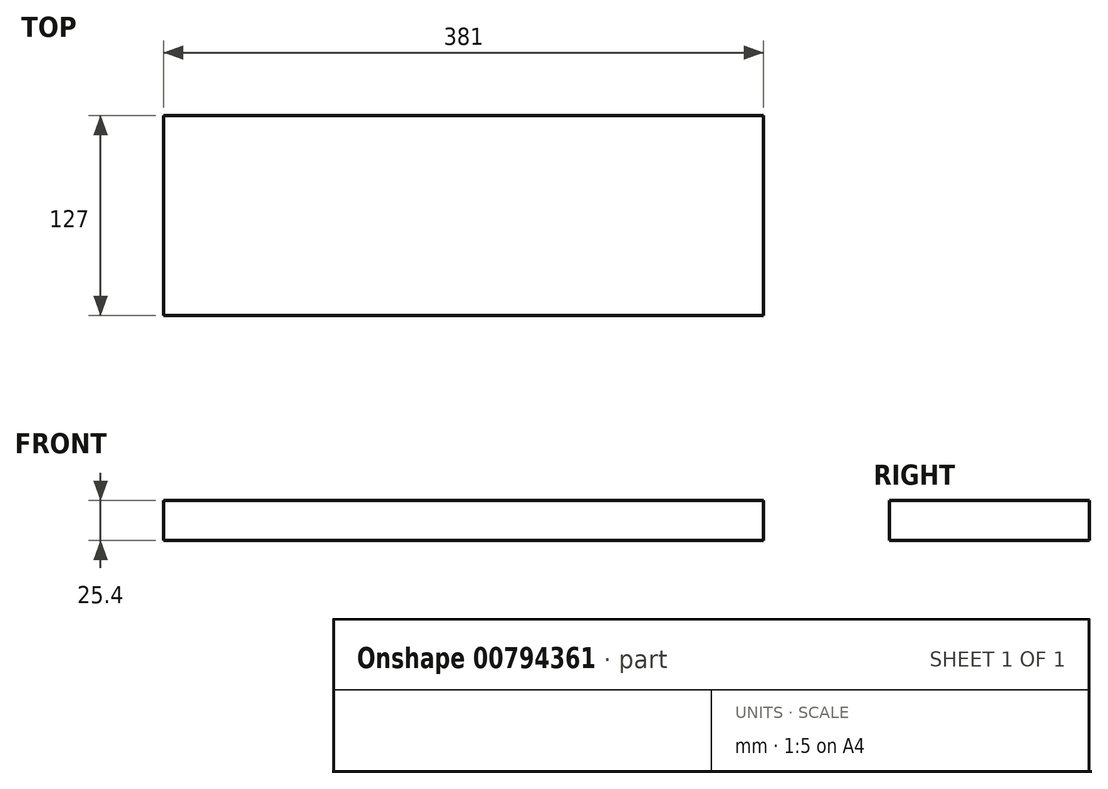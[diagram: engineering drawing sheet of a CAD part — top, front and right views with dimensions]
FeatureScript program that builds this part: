
annotation { "Feature Type Name" : "Feature", "Feature Type Description" : "" }
export const myFeature = defineFeature(function(context is Context, id is Id, definition is map)
    precondition{}
    {
        {
            var Q0;
            Q0=qCreatedBy(makeId("Top.planeOp"),FACE);
            var sketch = newSketch(context, id + "F0", { "sketchPlane" : qUnion([Q0])});
            skLineSegment(sketch, "E0.bottom", {"start": v(-125.96, 65.27) * mm, "end": v(255.04, 65.27) * mm});
            skLineSegment(sketch, "E0.top", {"start": v(-125.96, -61.73) * mm, "end": v(255.04, -61.73) * mm});
            skLineSegment(sketch, "E0.left", {"start": v(-125.96, 65.27) * mm, "end": v(-125.96, -61.73) * mm});
            skLineSegment(sketch, "E0.right", {"start": v(255.04, 65.27) * mm, "end": v(255.04, -61.73) * mm});
            skSolve(sketch);
        }
        {
            var Q0;
            Q0=makeQuery(id+"F0.imprint","IMPRINT",FACE,{"disambiguationData":[TD([[makeQuery(id+"F0.imprint","IMPRINT",EDGE,{"derivedFrom":sQuery(id+"F0.wireOp",EDGE,"E0.bottom")}),-1.0]])]});
            extrude(context, id + "F1", {"entities" : qUnion([Q0]), "depth" : 25.4 * mm, "offsetDistance" : 25.4 * mm});
        }
    });
